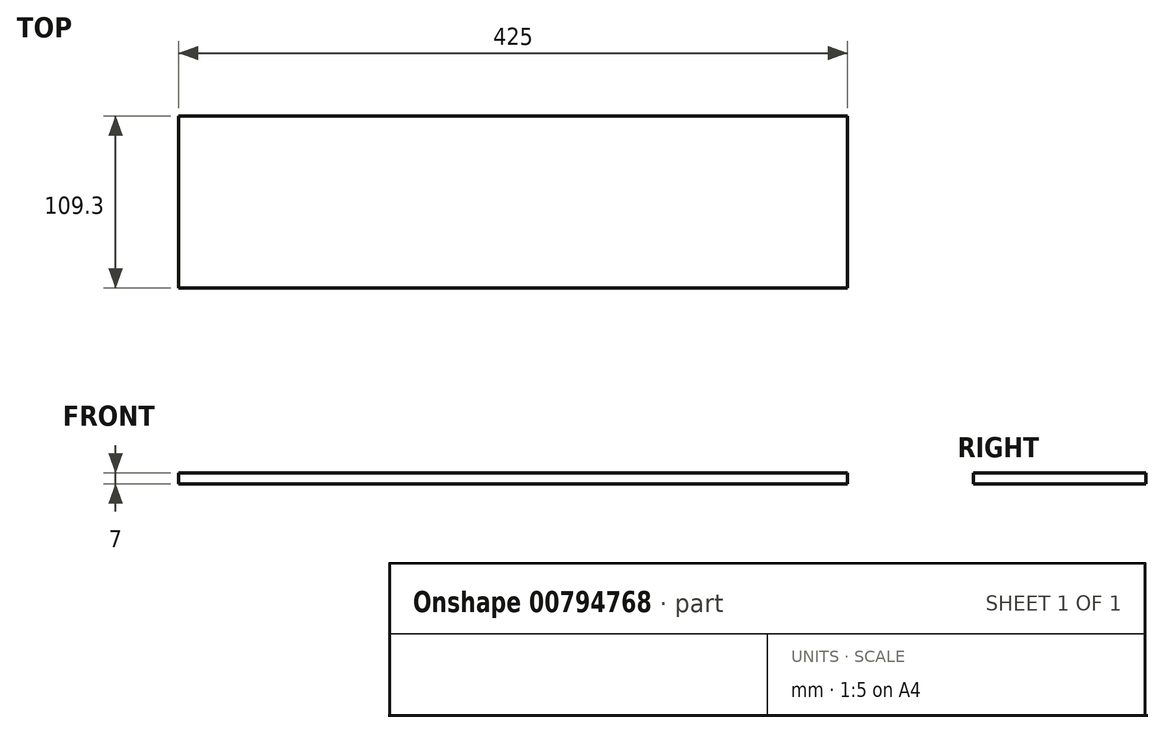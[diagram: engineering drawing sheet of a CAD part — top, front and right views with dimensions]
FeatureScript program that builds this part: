
annotation { "Feature Type Name" : "Feature", "Feature Type Description" : "" }
export const myFeature = defineFeature(function(context is Context, id is Id, definition is map)
    precondition{}
    {
        {
            var Q0;
            Q0=qCreatedBy(makeId("Top.planeOp"),FACE);
            var sketch = newSketch(context, id + "F0", { "sketchPlane" : qUnion([Q0])});
            skLineSegment(sketch, "E0.bottom", {"start": v(212.5, -54.65) * mm, "end": v(-212.5, -54.65) * mm});
            skLineSegment(sketch, "E0.top", {"start": v(212.5, 54.65) * mm, "end": v(-212.5, 54.65) * mm});
            skLineSegment(sketch, "E0.left", {"start": v(212.5, -54.65) * mm, "end": v(212.5, 54.65) * mm});
            skLineSegment(sketch, "E0.right", {"start": v(-212.5, -54.65) * mm, "end": v(-212.5, 54.65) * mm});
            skPoint(sketch, "E0.middle", {"position": v(0, 0) * mm});
            skSolve(sketch);
        }
        {
            var Q0;
            Q0=makeQuery(id+"F0.imprint","IMPRINT",FACE,{"disambiguationData":[TD([[makeQuery(id+"F0.imprint","IMPRINT",EDGE,{"derivedFrom":sQuery(id+"F0.wireOp",EDGE,"E0.bottom")}),-1.0]])]});
            extrude(context, id + "F1", {"entities" : qUnion([Q0]), "depth" : 7 * mm, "offsetDistance" : 25 * mm});
        }
    });
